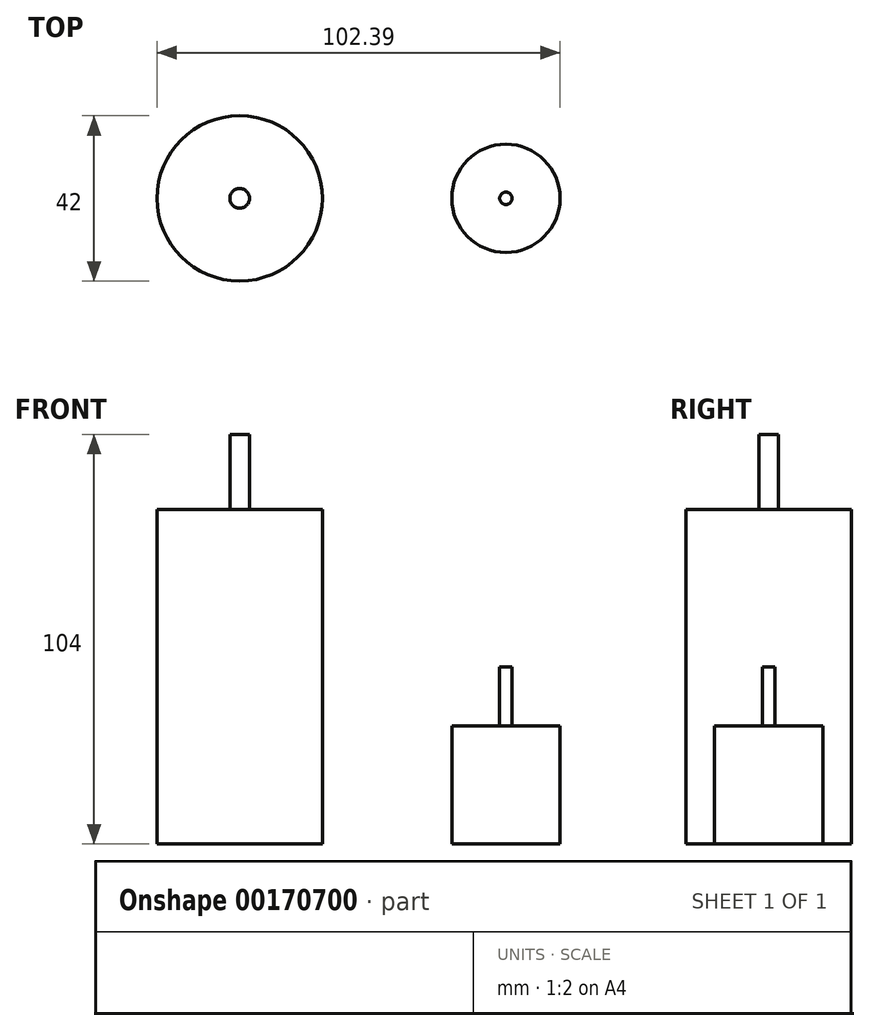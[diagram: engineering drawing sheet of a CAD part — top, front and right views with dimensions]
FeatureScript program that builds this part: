
annotation { "Feature Type Name" : "Feature", "Feature Type Description" : "" }
export const myFeature = defineFeature(function(context is Context, id is Id, definition is map)
    precondition{}
    {
        {
            var Q0;
            Q0=qCreatedBy(makeId("Top.planeOp"),FACE);
            var sketch = newSketch(context, id + "F0", { "sketchPlane" : qUnion([Q0])});
            skCircle(sketch, "E0", {"center": v(0, 0) * mm, "radius": 13.75 * mm});
            skSolve(sketch);
        }
        {
            var Q0;
            Q0=makeQuery(id+"F0.imprint","IMPRINT",FACE,{"disambiguationData":[TD([[makeQuery(id+"F0.imprint","IMPRINT",EDGE,{"derivedFrom":sQuery(id+"F0.wireOp",EDGE,"E0")}),1.0]])]});
            extrude(context, id + "F1", {"entities" : qUnion([Q0]), "depth" : 30 * mm});
        }
        {
            var Q0;
            Q0=makeQuery(id+"F1.opExtrude","CAP_FACE",FACE,{"disambiguationData":[OSD([sQuery(id+"F0.wireOp",EDGE,"E0")])],"isStart":false});
            var sketch = newSketch(context, id + "F2", { "sketchPlane" : qUnion([Q0])});
            skCircle(sketch, "E1", {"center": v(0, 0) * mm, "radius": 1.58 * mm});
            skSolve(sketch);
        }
        {
            var Q0;
            Q0 = qSketchRegion(id + "F2", true);
            extrude(context, id + "F3", {"entities" : qUnion([Q0]), "operationType" : NewBodyOperationType.ADD, "depth" : 15 * mm});
        }
        {
            var Q0;
            Q0=qCreatedBy(makeId("Top.planeOp"),FACE);
            var sketch = newSketch(context, id + "F4", { "sketchPlane" : qUnion([Q0])});
            skCircle(sketch, "E2", {"center": v(-67.64, 0) * mm, "radius": 21 * mm});
            skSolve(sketch);
        }
        {
            var Q0;
            Q0=makeQuery(id+"F4.imprint","IMPRINT",FACE,{"disambiguationData":[TD([[makeQuery(id+"F4.imprint","IMPRINT",EDGE,{"derivedFrom":sQuery(id+"F4.wireOp",EDGE,"E2")}),1.0]])]});
            extrude(context, id + "F5", {"entities" : qUnion([Q0]), "depth" : 85 * mm});
        }
        {
            var Q0;
            Q0=makeQuery(id+"F5.opExtrude","CAP_FACE",FACE,{"disambiguationData":[OSD([sQuery(id+"F4.wireOp",EDGE,"E2")])],"isStart":false});
            var sketch = newSketch(context, id + "F6", { "sketchPlane" : qUnion([Q0])});
            skCircle(sketch, "E3", {"center": v(-67.64, 0) * mm, "radius": 2.5 * mm});
            skSolve(sketch);
        }
        {
            var Q0;
            Q0 = qSketchRegion(id + "F6", true);
            extrude(context, id + "F7", {"entities" : qUnion([Q0]), "operationType" : NewBodyOperationType.ADD, "depth" : 19 * mm});
        }
    });
